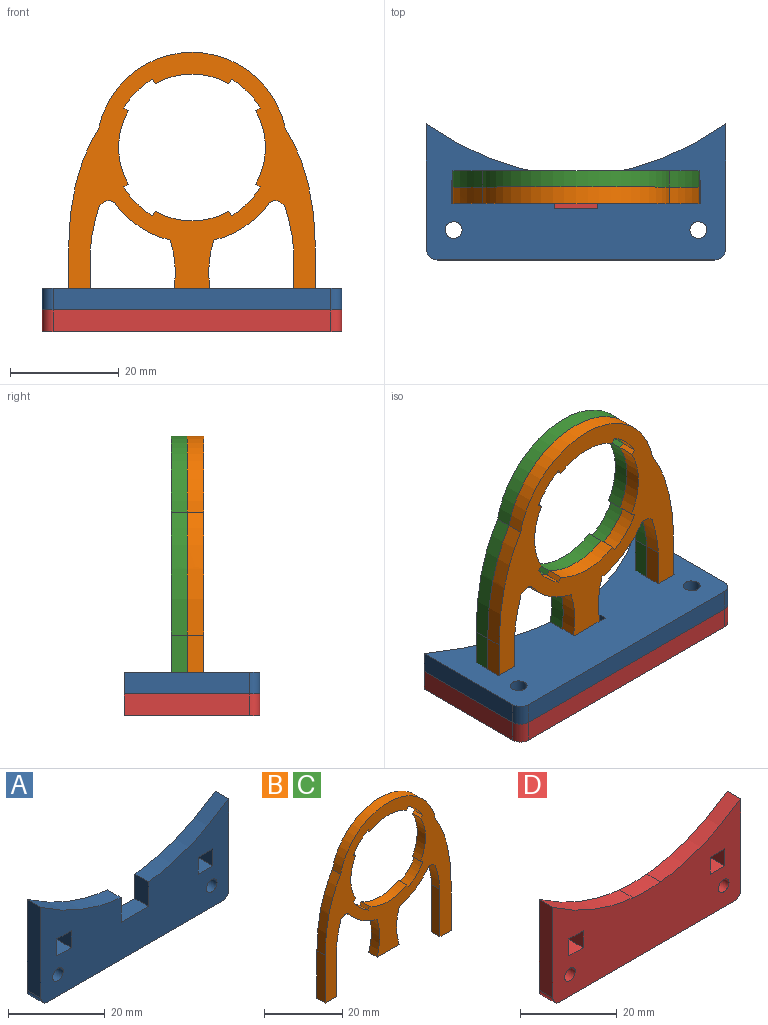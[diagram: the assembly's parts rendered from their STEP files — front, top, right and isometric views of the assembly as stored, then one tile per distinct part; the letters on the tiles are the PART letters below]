
ASSEMBLY  parts=4 mates=3
PART A: 22 faces, bbox 55x4x25 mm
  f0: plane 4.2x4mm, normal (0,0,1), area 16.8mm2, adj f1,f19,f20,f21
  f1: plane 4.3x4mm, normal (1,0,0), area 17.2mm2, adj f0,f2,f20,f21
  f2: plane 4.2x4mm, normal (0,0,-1), area 16.8mm2, adj f1,f19,f20,f21
  f3: extruded ~23.5x9.29mm, area 102.2mm2, adj f4,f15,f20,f21
  f4: plane 23x4mm, normal (-1,0,0), area 92mm2, adj f3,f5,f20,f21
  f5: cylinder r=2mm len=4mm, axis (0,1,0), area 12.6mm2, adj f4,f6,f20,f21
  f6: plane 51x4mm, normal (0,0,-1), area 204mm2, adj f5,f7,f20,f21
  f7: cylinder r=2mm len=4mm, axis (0,1,0), area 12.6mm2, adj f6,f8,f20,f21
  f8: plane 23x4mm, normal (1,0,0), area 92mm2, adj f7,f9,f20,f21
  f9: extruded ~23.5x9.29mm, area 102.2mm2, adj f8,f10,f20,f21
  f10: plane 6.21x4mm, normal (-1,0,0), area 24.8mm2, adj f9,f11,f20,f21
  f11: plane 8x4mm, normal (0,0,1), area 32mm2, adj f10,f15,f20,f21
  f12: plane 4.2x4mm, normal (0,0,-1), area 16.8mm2, adj f13,f18,f20,f21
  f13: plane 4.3x4mm, normal (-1,0,0), area 17.2mm2, adj f12,f14,f20,f21
  f14: plane 4.2x4mm, normal (0,0,1), area 16.8mm2, adj f13,f18,f20,f21
  f15: plane 6.21x4mm, normal (1,0,0), area 24.8mm2, adj f3,f11,f20,f21
  f16: cylinder r=1.55mm len=4mm, axis (0,1,0), area 39mm2, adj f20,f21
  f17: cylinder r=1.55mm len=4mm, axis (0,1,0), area 39mm2, adj f20,f21
  f18: plane 4.3x4mm, normal (1,0,0), area 17.2mm2, adj f12,f14,f20,f21
  f19: plane 4.3x4mm, normal (-1,0,0), area 17.2mm2, adj f0,f2,f20,f21
  f20: plane 55x25mm, normal (0,-1,0), area 925.4mm2, adj f0,f1,f2,f3,f4,f5,f6,f7
  f21: plane 55x25mm, normal (0,1,0), area 925.4mm2, adj f0,f1,f2,f3,f4,f5,f6,f7
PART B: 36 faces, bbox 45.4x3x51.4 mm
  f0: plane 14.83x3mm, normal (-1,0,0), area 44.5mm2, adj f1,f33,f34,f35
  f1: plane 4x3mm, normal (0,0,-1), area 12mm2, adj f0,f2,f34,f35
  f2: plane 14.83x3mm, normal (1,0,0), area 44.5mm2, adj f1,f3,f34,f35
  f3: extruded ~8.42x3mm, area 25.8mm2, adj f2,f4,f34,f35
  f4: extruded ~3.13x3mm, area 11mm2, adj f3,f5,f34,f35
  f5: cylinder r=17.5mm len=9.91mm, axis (0,1,0), area 36.2mm2, adj f4,f6,f34,f35
  f6: extruded ~11.82x3mm, area 36mm2, adj f5,f7,f34,f35
  f7: plane 8x3mm, normal (0,0,-1), area 24mm2, adj f6,f8,f34,f35
  f8: extruded ~11.82x3mm, area 36mm2, adj f7,f9,f34,f35
  f9: cylinder r=17.5mm len=9.91mm, axis (0,1,0), area 36.2mm2, adj f8,f10,f34,f35
  f10: extruded ~3.13x3mm, area 11mm2, adj f9,f11,f34,f35
  f11: extruded ~8.42x3mm, area 25.8mm2, adj f10,f12,f34,f35
  f12: plane 14.83x3mm, normal (-1,0,0), area 44.5mm2, adj f11,f13,f34,f35
  f13: plane 4x3mm, normal (0,0,-1), area 12mm2, adj f12,f14,f34,f35
  f14: plane 14.83x3mm, normal (1,0,0), area 44.5mm2, adj f13,f15,f34,f35
  f15: extruded ~22.61x5.58mm, area 70.8mm2, adj f14,f16,f34,f35
  f16: cylinder r=17.5mm len=34.26mm, axis (0,1,0), area 143.3mm2, adj f15,f33,f34,f35
  f17: cylinder r=14.5mm len=5.31mm, axis (0,1,0), area 22.8mm2, adj f18,f32,f34,f35
  f18: plane 3x0.87mm, normal (-0.5,0,0.87), area 3mm2, adj f17,f19,f34,f35
  f19: cylinder r=13.5mm len=13.5mm, axis (0,1,0), area 42.4mm2, adj f18,f20,f34,f35
  f20: plane 3x0.87mm, normal (-0.5,0,-0.87), area 3mm2, adj f19,f21,f34,f35
  f21: cylinder r=14.5mm len=5.31mm, axis (0,1,0), area 22.8mm2, adj f20,f22,f34,f35
  f22: plane 3x0.87mm, normal (0.87,0,0.5), area 3mm2, adj f21,f23,f34,f35
  f23: cylinder r=13.5mm len=13.5mm, axis (0,1,0), area 42.4mm2, adj f22,f24,f34,f35
  f24: plane 3x0.87mm, normal (-0.87,0,0.5), area 3mm2, adj f23,f25,f34,f35
  f25: cylinder r=14.5mm len=5.31mm, axis (0,1,0), area 22.8mm2, adj f24,f26,f34,f35
  f26: plane 3x0.87mm, normal (0.5,0,-0.87), area 3mm2, adj f25,f27,f34,f35
  f27: cylinder r=13.5mm len=13.5mm, axis (0,1,0), area 42.4mm2, adj f26,f28,f34,f35
  f28: plane 3x0.87mm, normal (0.5,0,0.87), area 3mm2, adj f27,f29,f34,f35
  f29: cylinder r=14.5mm len=5.31mm, axis (0,1,0), area 22.8mm2, adj f28,f30,f34,f35
  f30: plane 3x0.87mm, normal (-0.87,0,-0.5), area 3mm2, adj f29,f31,f34,f35
  f31: cylinder r=13.5mm len=13.5mm, axis (0,1,0), area 42.4mm2, adj f30,f32,f34,f35
  f32: plane 3x0.87mm, normal (0.87,0,-0.5), area 3mm2, adj f17,f31,f34,f35
  f33: extruded ~22.61x5.58mm, area 70.8mm2, adj f0,f16,f34,f35
  f34: plane 51.36x45.43mm, normal (0,-1,0), area 729.5mm2, adj f0,f1,f2,f3,f4,f5,f6,f7
  f35: plane 51.36x45.43mm, normal (0,1,0), area 729.5mm2, adj f0,f1,f2,f3,f4,f5,f6,f7
PART C: same geometry as B
PART D: 20 faces, bbox 55x4x25 mm
  f0: plane 4.2x4mm, normal (0,0,1), area 16.8mm2, adj f1,f17,f18,f19
  f1: plane 4.3x4mm, normal (1,0,0), area 17.2mm2, adj f0,f2,f18,f19
  f2: plane 4.2x4mm, normal (0,0,-1), area 16.8mm2, adj f1,f17,f18,f19
  f3: cylinder r=2mm len=4mm, axis (0,1,0), area 12.6mm2, adj f4,f13,f18,f19
  f4: plane 51x4mm, normal (0,0,-1), area 204mm2, adj f3,f5,f18,f19
  f5: cylinder r=2mm len=4mm, axis (0,1,0), area 12.6mm2, adj f4,f6,f18,f19
  f6: plane 23x4mm, normal (1,0,0), area 92mm2, adj f5,f7,f18,f19
  f7: extruded ~23.5x9.29mm, area 102.2mm2, adj f6,f8,f18,f19
  f8: extruded ~8x4mm, area 32.1mm2, adj f7,f9,f18,f19
  f9: extruded ~23.5x9.29mm, area 102.2mm2, adj f8,f13,f18,f19
  f10: plane 4.2x4mm, normal (0,0,-1), area 16.8mm2, adj f11,f16,f18,f19
  f11: plane 4.3x4mm, normal (-1,0,0), area 17.2mm2, adj f10,f12,f18,f19
  f12: plane 4.2x4mm, normal (0,0,1), area 16.8mm2, adj f11,f16,f18,f19
  f13: plane 23x4mm, normal (-1,0,0), area 92mm2, adj f3,f9,f18,f19
  f14: cylinder r=1.55mm len=4mm, axis (0,1,0), area 39mm2, adj f18,f19
  f15: cylinder r=1.55mm len=4mm, axis (0,1,0), area 39mm2, adj f18,f19
  f16: plane 4.3x4mm, normal (1,0,0), area 17.2mm2, adj f10,f12,f18,f19
  f17: plane 4.3x4mm, normal (-1,0,0), area 17.2mm2, adj f0,f2,f18,f19
  f18: plane 55x25mm, normal (0,-1,0), area 974mm2, adj f0,f1,f2,f3,f4,f5,f6,f7
  f19: plane 55x25mm, normal (0,1,0), area 974mm2, adj f0,f1,f2,f3,f4,f5,f6,f7
PLACE A rot(axis=(-1,0,0),90deg) t=(15.22,-6.48,-34.7)mm
PLACE B t=(-12.28,-5.63,-4.83)mm
PLACE C t=(-12.28,-2.63,-4.83)mm fixed
PLACE D rot(axis=(-1,0,0),90deg) t=(15.22,-6.48,-38.7)mm
MATE fastened B.f34 <-> D.f0  axis (0,-1,0) through (-32.99,-8.63,-38.7)mm
MATE fastened C.f34 <-> B.f35  axis (0,-1,0) through (-32.99,-5.63,-38.7)mm
MATE fastened A.f21 <-> D.f18  axis (0,0,-1) through (-12.28,-18.98,-34.7)mm
